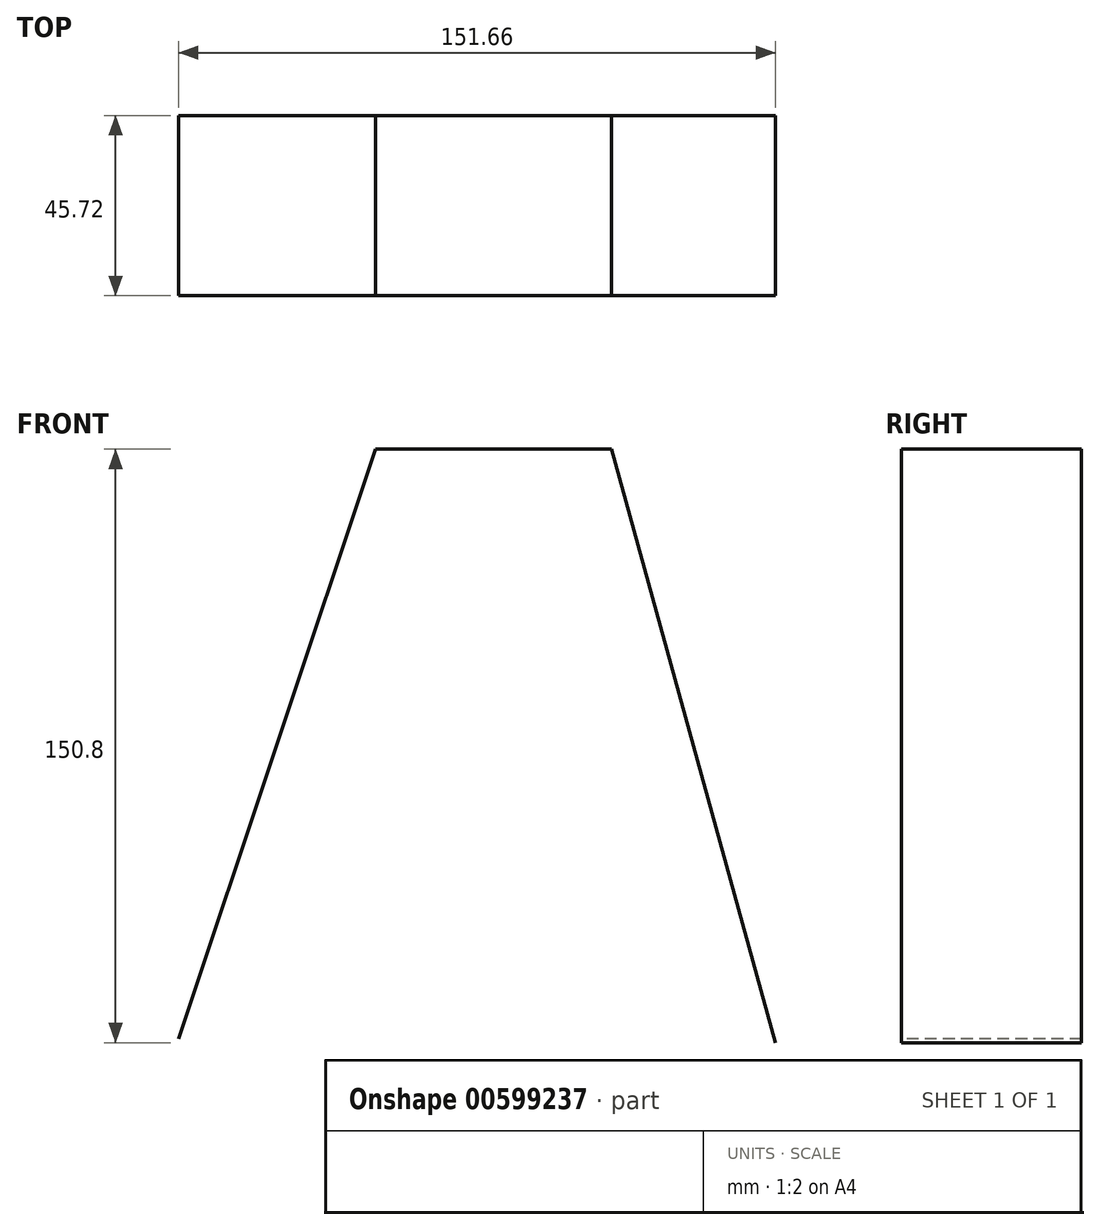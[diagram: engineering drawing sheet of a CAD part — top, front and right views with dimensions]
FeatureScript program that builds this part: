
annotation { "Feature Type Name" : "Feature", "Feature Type Description" : "" }
export const myFeature = defineFeature(function(context is Context, id is Id, definition is map)
    precondition{}
    {
        {
            var Q0;
            Q0=qCreatedBy(makeId("Front.planeOp"),FACE);
            var sketch = newSketch(context, id + "F0", { "sketchPlane" : qUnion([Q0])});
            skLineSegment(sketch, "E0", {"start": v(-76.05, -75) * mm, "end": v(-26.08, 74.88) * mm});
            skLineSegment(sketch, "E1", {"start": v(33.97, 74.88) * mm, "end": v(75.61, -75.92) * mm});
            skLineSegment(sketch, "E2", {"start": v(-26.08, 74.88) * mm, "end": v(33.97, 74.88) * mm});
            skSolve(sketch);
        }
        {
            var Q0;
            Q0=sQuery(id+"F0.wireOp",EDGE,"E0");
            var Q1;
            Q1=sQuery(id+"F0.wireOp",EDGE,"E2");
            var Q2;
            Q2=sQuery(id+"F0.wireOp",EDGE,"E1");
            extrude(context, id + "F1", {"bodyType" : ToolBodyType.SURFACE, "surfaceEntities" : qUnion([Q0, Q1, Q2]), "depth" : 45.72 * mm, "offsetDistance" : 25.4 * mm});
        }
    });
